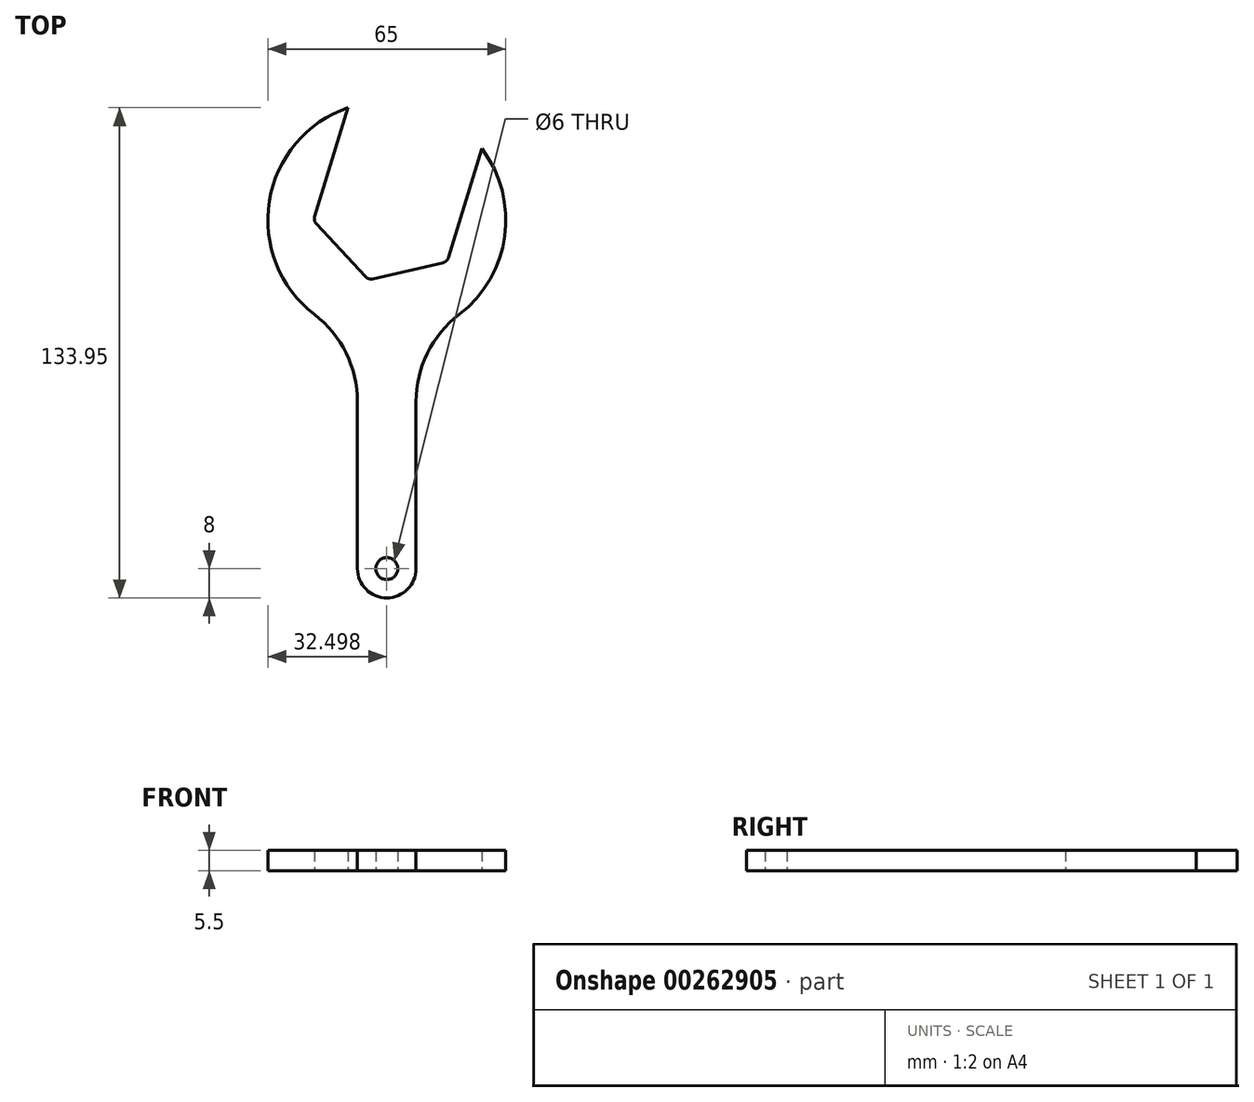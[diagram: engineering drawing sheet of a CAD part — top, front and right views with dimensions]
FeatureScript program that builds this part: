
annotation { "Feature Type Name" : "Feature", "Feature Type Description" : "" }
export const myFeature = defineFeature(function(context is Context, id is Id, definition is map)
    precondition{}
    {
        {
            var Q0;
            Q0=qCreatedBy(makeId("Top.planeOp"),FACE);
            var sketch = newSketch(context, id + "F0", { "sketchPlane" : qUnion([Q0])});
            skCircle(sketch, "E0.cCircle", {"center": v(0, 0) * mm, "radius": 19.1 * mm, "construction": true});
            skLineSegment(sketch, "E0.0", {"start": v(24.5, 14.78) * mm, "end": v(15.38, -15.03) * mm});
            skLineSegment(sketch, "E0.1", {"start": v(13.92, -16.39) * mm, "end": v(-5.32, -20.83) * mm});
            skLineSegment(sketch, "E0.2", {"start": v(-7.24, -20.25) * mm, "end": v(-20.7, -5.8) * mm});
            skLineSegment(sketch, "E0.3", {"start": v(-21.15, -3.86) * mm, "end": v(-12.04, 25.95) * mm});
            skLineSegment(sketch, "E0.4", {"start": v(-15.04, 16.13) * mm, "end": v(6.45, 21.1) * mm, "construction": true});
            skLineSegment(sketch, "E0.5", {"start": v(6.45, 21.1) * mm, "end": v(21.49, 4.96) * mm, "construction": true});
            skPoint(sketch, "E0.0.midPoint", {"position": v(18.27, -5.58) * mm});
            skArc(sketch, "E1", {"start": v(-9.46, -100) * mm, "mid": v(-1.46, -108) * mm, "end": v(6.54, -100) * mm});
            skLineSegment(sketch, "E2.trimOffspring", {"start": v(6.54, -54.4) * mm, "end": v(6.54, -100) * mm});
            skLineSegment(sketch, "E3.trimOffspring", {"start": v(-9.46, -54.4) * mm, "end": v(-9.46, -100) * mm});
            skCircle(sketch, "E4", {"center": v(-1.46, -100) * mm, "radius": 3 * mm});
            skPoint(sketch, "E5.visualSharp", {"position": v(21.49, 4.96) * mm});
            skPoint(sketch, "E6.visualSharp", {"position": v(-15.04, 16.13) * mm});
            skLineSegment(sketch, "E7", {"start": v(-5.58, -18.27) * mm, "end": v(5.58, 18.27) * mm, "construction": true});
            skArc(sketch, "E8", {"start": v(18.3, -30.58) * mm, "mid": v(30.74, -9.18) * mm, "end": v(24.5, 14.78) * mm});
            skArc(sketch, "E9", {"start": v(-9.46, -36.28) * mm, "mid": v(-1.46, -37.28) * mm, "end": v(6.54, -36.28) * mm, "construction": true});
            skLineSegment(sketch, "E10", {"start": v(-1.46, -4.78) * mm, "end": v(-1.46, -100) * mm, "construction": true});
            skLineSegment(sketch, "E11", {"start": v(-12.04, 25.95) * mm, "end": v(-12.04, 25.95) * mm});
            skArc(sketch, "E12", {"start": v(-12.04, 25.95) * mm, "mid": v(-33.54, 0.43) * mm, "end": v(-21.22, -30.58) * mm});
            skArc(sketch, "E13", {"start": v(24.5, 14.78) * mm, "mid": v(8.04, 26.3) * mm, "end": v(-12.04, 25.95) * mm, "construction": true});
            skPoint(sketch, "E14.visualSharp", {"position": v(6.54, -36.28) * mm});
            skArc(sketch, "E14.filletArc", {"start": v(18.3, -30.58) * mm, "mid": v(9.64, -41.12) * mm, "end": v(6.54, -54.4) * mm});
            skPoint(sketch, "E15.visualSharp", {"position": v(-9.46, -36.28) * mm});
            skArc(sketch, "E15.filletArc", {"start": v(-9.46, -54.4) * mm, "mid": v(-12.56, -41.12) * mm, "end": v(-21.22, -30.58) * mm});
            skPoint(sketch, "E16.visualSharp", {"position": v(-21.49, -4.96) * mm});
            skArc(sketch, "E16.filletArc", {"start": v(-21.15, -3.86) * mm, "mid": v(-21.19, -4.9) * mm, "end": v(-20.7, -5.8) * mm});
            skPoint(sketch, "E17.visualSharp", {"position": v(-6.45, -21.1) * mm});
            skArc(sketch, "E17.filletArc", {"start": v(-7.24, -20.25) * mm, "mid": v(-6.36, -20.8) * mm, "end": v(-5.32, -20.83) * mm});
            skPoint(sketch, "E18.visualSharp", {"position": v(15.04, -16.13) * mm});
            skArc(sketch, "E18.filletArc", {"start": v(13.92, -16.39) * mm, "mid": v(14.83, -15.9) * mm, "end": v(15.38, -15.03) * mm});
            skSolve(sketch);
        }
        {
            var Q0;
            Q0=qSketchRegion(id+"F0",true);
            extrude(context, id + "F1", {"entities" : qUnion([Q0]), "depth" : 5.5 * mm});
        }
    });
